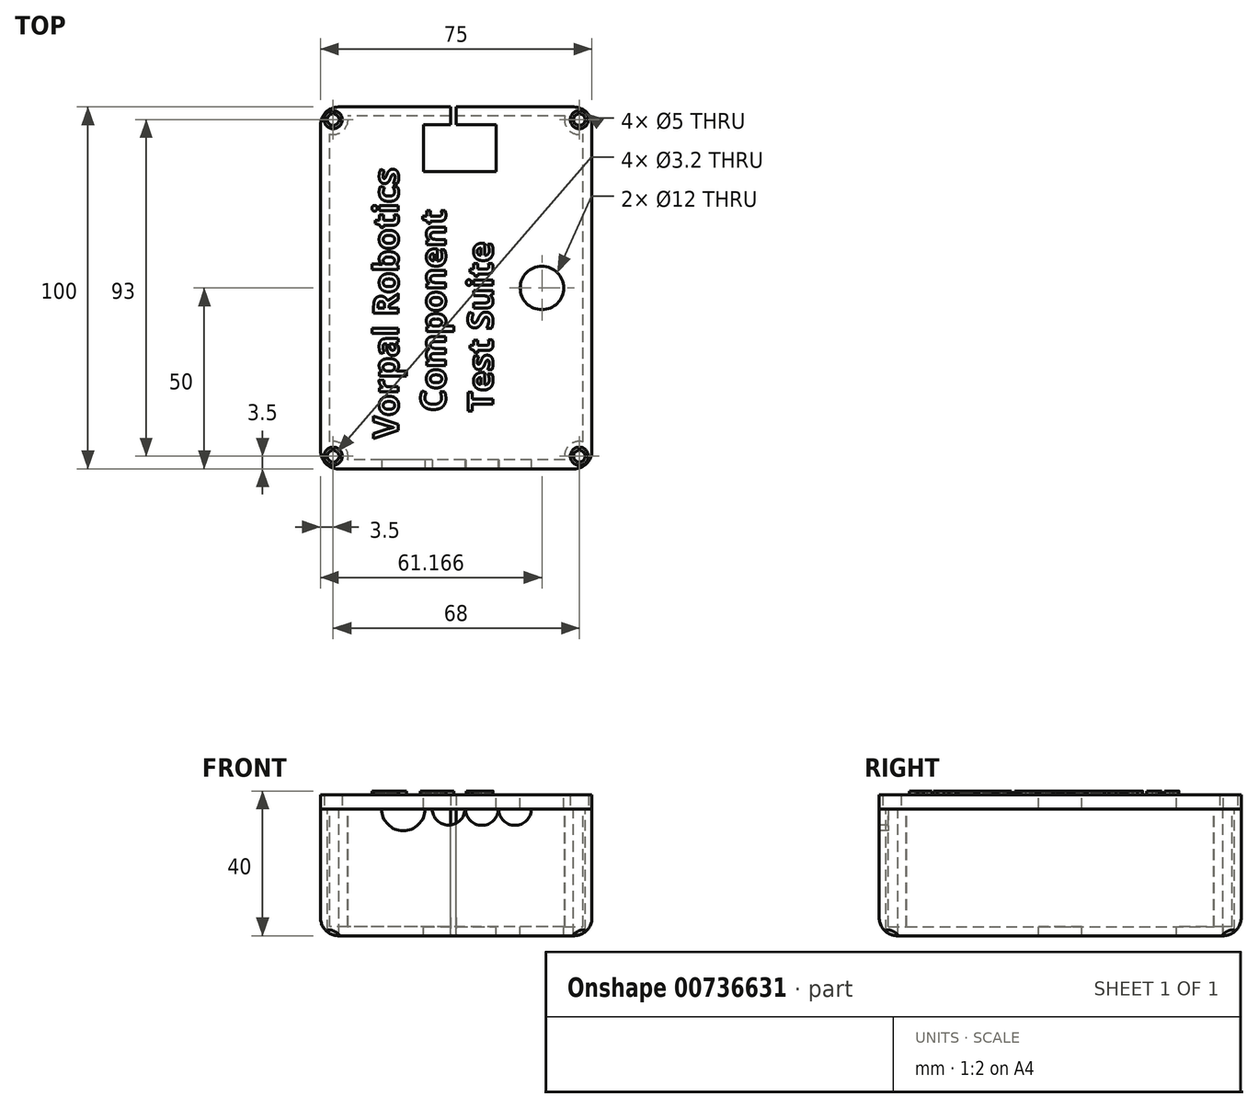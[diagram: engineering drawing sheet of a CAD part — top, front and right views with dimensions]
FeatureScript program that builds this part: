
annotation { "Feature Type Name" : "Feature", "Feature Type Description" : "" }
export const myFeature = defineFeature(function(context is Context, id is Id, definition is map)
    precondition{}
    {
        {
            var Q0;
            Q0=qCreatedBy(makeId("Top.planeOp"),FACE);
            var sketch = newSketch(context, id + "F0", { "sketchPlane" : qUnion([Q0])});
            skLineSegment(sketch, "E0.bottom", {"start": v(37.5, -50) * mm, "end": v(-37.5, -50) * mm});
            skLineSegment(sketch, "E0.top", {"start": v(37.5, 50) * mm, "end": v(-37.5, 50) * mm});
            skLineSegment(sketch, "E0.left", {"start": v(37.5, -50) * mm, "end": v(37.5, 50) * mm});
            skLineSegment(sketch, "E0.right", {"start": v(-37.5, -50) * mm, "end": v(-37.5, 50) * mm});
            skPoint(sketch, "E0.middle", {"position": v(0, 0) * mm});
            skLineSegment(sketch, "E1.bottom", {"start": v(34, -46.5) * mm, "end": v(-34, -46.5) * mm, "construction": true});
            skLineSegment(sketch, "E1.top", {"start": v(34, 46.5) * mm, "end": v(-34, 46.5) * mm, "construction": true});
            skLineSegment(sketch, "E1.left", {"start": v(34, -46.5) * mm, "end": v(34, 46.5) * mm, "construction": true});
            skLineSegment(sketch, "E1.right", {"start": v(-34, -46.5) * mm, "end": v(-34, 46.5) * mm, "construction": true});
            skCircle(sketch, "E2", {"center": v(-34, 46.5) * mm, "radius": 2.5 * mm});
            skCircle(sketch, "E3", {"center": v(34, 46.5) * mm, "radius": 2.5 * mm});
            skCircle(sketch, "E4", {"center": v(-34, -46.5) * mm, "radius": 2.5 * mm});
            skCircle(sketch, "E5", {"center": v(34, -46.5) * mm, "radius": 2.5 * mm});
            skCircle(sketch, "E6", {"center": v(-34, 46.5) * mm, "radius": 1.6 * mm});
            skCircle(sketch, "E7", {"center": v(34, 46.5) * mm, "radius": 1.6 * mm});
            skCircle(sketch, "E8", {"center": v(34, -46.5) * mm, "radius": 1.6 * mm});
            skCircle(sketch, "E9", {"center": v(-34, -46.5) * mm, "radius": 1.6 * mm});
            skSolve(sketch);
        }
        {
            var Q0;
            Q0 = qSketchRegion(id + "F0", true);
            var Q1;
            Q1=makeQuery(id+"F0.imprint","IMPRINT",FACE,{"disambiguationData":[TD([[makeQuery(id+"F0.imprint","IMPRINT",EDGE,{"derivedFrom":sQuery(id+"F0.wireOp",EDGE,"E2")}),1.0]])]});
            var Q2;
            Q2=makeQuery(id+"F0.imprint","IMPRINT",FACE,{"disambiguationData":[TD([[makeQuery(id+"F0.imprint","IMPRINT",EDGE,{"derivedFrom":sQuery(id+"F0.wireOp",EDGE,"E3")}),1.0]])]});
            var Q3;
            Q3=makeQuery(id+"F0.imprint","IMPRINT",FACE,{"disambiguationData":[TD([[makeQuery(id+"F0.imprint","IMPRINT",EDGE,{"derivedFrom":sQuery(id+"F0.wireOp",EDGE,"E4")}),1.0]])]});
            var Q4;
            Q4=makeQuery(id+"F0.imprint","IMPRINT",FACE,{"disambiguationData":[TD([[makeQuery(id+"F0.imprint","IMPRINT",EDGE,{"derivedFrom":sQuery(id+"F0.wireOp",EDGE,"E5")}),1.0]])]});
            extrude(context, id + "F1", {"entities" : qUnion([Q0, Q1, Q2, Q3, Q4]), "oppositeDirection" : true, "depth" : 35 * mm, "offsetDistance" : 25 * mm});
        }
        {
            var Q0;
            Q0=makeQuery(id+"F1.opExtrude","CAP_FACE",FACE,{"disambiguationData":[OSD([sQuery(id+"F0.wireOp",EDGE,"E0.bottom"),sQuery(id+"F0.wireOp",EDGE,"E0.top"),sQuery(id+"F0.wireOp",EDGE,"E0.left"),sQuery(id+"F0.wireOp",EDGE,"E0.right"),sQuery(id+"F0.wireOp",EDGE,"E6"),sQuery(id+"F0.wireOp",EDGE,"E7"),sQuery(id+"F0.wireOp",EDGE,"E8"),sQuery(id+"F0.wireOp",EDGE,"E9")])],"isStart":true});
            shell(context, id + "F2", {"entities" : qUnion([Q0]), "thickness" : 2.5 * mm});
        }
        {
            var Q0;
            Q0=makeQuery(id+"F1.opExtrude","SWEPT_EDGE",EDGE,{"disambiguationData":[OSD([sQuery(id+"F0.wireOp",EDGE,"E0.bottom"),sQuery(id+"F0.wireOp",EDGE,"E0.right")])]});
            var Q1;
            Q1=makeQuery(id+"F1.opExtrude","SWEPT_EDGE",EDGE,{"disambiguationData":[OSD([sQuery(id+"F0.wireOp",EDGE,"E0.bottom"),sQuery(id+"F0.wireOp",EDGE,"E0.left")])]});
            var Q2;
            Q2=makeQuery(id+"F1.opExtrude","SWEPT_EDGE",EDGE,{"disambiguationData":[OSD([sQuery(id+"F0.wireOp",EDGE,"E0.top"),sQuery(id+"F0.wireOp",EDGE,"E0.left")])]});
            var Q3;
            Q3=makeQuery(id+"F1.opExtrude","SWEPT_EDGE",EDGE,{"disambiguationData":[OSD([sQuery(id+"F0.wireOp",EDGE,"E0.top"),sQuery(id+"F0.wireOp",EDGE,"E0.right")])]});
            var Q4;
            Q4=makeQuery(id+"F1.opExtrude","CAP_EDGE",EDGE,{"disambiguationData":[OSD([sQuery(id+"F0.wireOp",EDGE,"E0.top")])],"isStart":false});
            var Q5;
            Q5=makeQuery(id+"F1.opExtrude","CAP_EDGE",EDGE,{"disambiguationData":[OSD([sQuery(id+"F0.wireOp",EDGE,"E0.right")])],"isStart":false});
            var Q6;
            Q6=makeQuery(id+"F1.opExtrude","CAP_EDGE",EDGE,{"disambiguationData":[OSD([sQuery(id+"F0.wireOp",EDGE,"E0.bottom")])],"isStart":false});
            var Q7;
            Q7=makeQuery(id+"F1.opExtrude","CAP_EDGE",EDGE,{"disambiguationData":[OSD([sQuery(id+"F0.wireOp",EDGE,"E0.left")])],"isStart":false});
            fillet(context, id + "F3", {"entities" : qUnion([Q0, Q1, Q2, Q3, Q4, Q5, Q6, Q7]), "radius" : 5 * mm, "allowEdgeOverflow" : false});
        }
        {
            var Q0;
            Q0=makeQuery(id+"F1.opExtrude","SWEPT_FACE",FACE,{"disambiguationData":[OSD([sQuery(id+"F0.wireOp",EDGE,"E0.bottom")])]});
            var sketch = newSketch(context, id + "F4", { "sketchPlane" : qUnion([Q0])});
            skCircle(sketch, "E10", {"center": v(-14.63, 0) * mm, "radius": 6 * mm});
            skCircle(sketch, "E11", {"center": v(-2.11, 0.07) * mm, "radius": 4.5 * mm});
            skCircle(sketch, "E12", {"center": v(7.1, 0) * mm, "radius": 4.5 * mm});
            skCircle(sketch, "E13", {"center": v(16.23, 0) * mm, "radius": 4.5 * mm});
            skSolve(sketch);
        }
        {
            var Q0;
            Q0 = qSketchRegion(id + "F4", true);
            extrude(context, id + "F5", {"entities" : qUnion([Q0]), "operationType" : NewBodyOperationType.REMOVE, "oppositeDirection" : true, "depth" : 25 * mm, "offsetDistance" : 25 * mm});
        }
        {
            var Q0;
            Q0 = qSketchRegion(id + "F0", true);
            extrude(context, id + "F6", {"entities" : qUnion([Q0]), "depth" : 4 * mm, "offsetDistance" : 25 * mm});
        }
        {
            var Q0;
            Q0=makeQuery(id+"F6.opExtrude","SWEPT_EDGE",EDGE,{"disambiguationData":[OSD([sQuery(id+"F0.wireOp",EDGE,"E0.bottom"),sQuery(id+"F0.wireOp",EDGE,"E0.right")])]});
            var Q1;
            Q1=makeQuery(id+"F6.opExtrude","SWEPT_EDGE",EDGE,{"disambiguationData":[OSD([sQuery(id+"F0.wireOp",EDGE,"E0.bottom"),sQuery(id+"F0.wireOp",EDGE,"E0.left")])]});
            var Q2;
            Q2=makeQuery(id+"F6.opExtrude","SWEPT_EDGE",EDGE,{"disambiguationData":[OSD([sQuery(id+"F0.wireOp",EDGE,"E0.top"),sQuery(id+"F0.wireOp",EDGE,"E0.left")])]});
            var Q3;
            Q3=makeQuery(id+"F6.opExtrude","SWEPT_EDGE",EDGE,{"disambiguationData":[OSD([sQuery(id+"F0.wireOp",EDGE,"E0.top"),sQuery(id+"F0.wireOp",EDGE,"E0.right")])]});
            fillet(context, id + "F7", {"entities" : qUnion([Q0, Q1, Q2, Q3]), "radius" : 5 * mm, "tangentPropagation" : true, "allowEdgeOverflow" : false});
        }
        {
            var Q0;
            Q0=makeQuery(id+"F6.opExtrude","CAP_FACE",FACE,{"disambiguationData":[OSD([sQuery(id+"F0.wireOp",EDGE,"E0.bottom"),sQuery(id+"F0.wireOp",EDGE,"E0.top"),sQuery(id+"F0.wireOp",EDGE,"E0.left"),sQuery(id+"F0.wireOp",EDGE,"E0.right"),sQuery(id+"F0.wireOp",EDGE,"E2"),sQuery(id+"F0.wireOp",EDGE,"E3"),sQuery(id+"F0.wireOp",EDGE,"E4"),sQuery(id+"F0.wireOp",EDGE,"E5")])],"isStart":false});
            var sketch = newSketch(context, id + "F8", { "sketchPlane" : qUnion([Q0])});
            skLineSegment(sketch, "E14.bottom", {"start": v(-8.99, 45.1) * mm, "end": v(-1.5, 45.1) * mm});
            skLineSegment(sketch, "E14.top", {"start": v(-8.99, 32.1) * mm, "end": v(11.01, 32.1) * mm});
            skLineSegment(sketch, "E14.left", {"start": v(-8.99, 45.1) * mm, "end": v(-8.99, 32.1) * mm});
            skLineSegment(sketch, "E14.right", {"start": v(11.01, 45.1) * mm, "end": v(11.01, 32.1) * mm});
            skLineSegment(sketch, "E15.bottom", {"start": v(-1.5, 53.63) * mm, "end": v(0, 53.63) * mm});
            skLineSegment(sketch, "E15.left", {"start": v(-1.5, 53.63) * mm, "end": v(-1.5, 45.1) * mm});
            skLineSegment(sketch, "E15.right", {"start": v(0, 53.63) * mm, "end": v(0, 45.1) * mm});
            skLineSegment(sketch, "E16.trimOffspring", {"start": v(0, 45.1) * mm, "end": v(11.01, 45.1) * mm});
            skCircle(sketch, "E17", {"center": v(23.67, 0) * mm, "radius": 6 * mm});
            skPoint(sketch, "E17.centerSnap0", {"position": v(37.5, 0) * mm});
            skSolve(sketch);
        }
        {
            var Q0;
            Q0 = qSketchRegion(id + "F8", true);
            extrude(context, id + "F9", {"entities" : qUnion([Q0]), "operationType" : NewBodyOperationType.REMOVE, "endBound" : BoundingType.THROUGH_ALL, "oppositeDirection" : true, "depth" : 25 * mm, "offsetDistance" : 25 * mm});
        }
        {
            var Q0;
            Q0=makeQuery(id+"F6.opExtrude","CAP_FACE",FACE,{"disambiguationData":[OSD([sQuery(id+"F0.wireOp",EDGE,"E0.bottom"),sQuery(id+"F0.wireOp",EDGE,"E0.top"),sQuery(id+"F0.wireOp",EDGE,"E0.left"),sQuery(id+"F0.wireOp",EDGE,"E0.right"),sQuery(id+"F0.wireOp",EDGE,"E2"),sQuery(id+"F0.wireOp",EDGE,"E3"),sQuery(id+"F0.wireOp",EDGE,"E4"),sQuery(id+"F0.wireOp",EDGE,"E5")])],"isStart":false});
            var sketch = newSketch(context, id + "F10", { "sketchPlane" : qUnion([Q0])});
            skText(sketch, "E18", { "text": "Vorpal Robotics\n   Component\n   Test Suite", "fontName": "OpenSans-Bold.ttf"});
            const initialGuessF10  = {"E18": [-0.01598, -0.04165, 0, 1, 0.0069]};
            skSetInitialGuess(sketch, initialGuessF10);
            skSolve(sketch);
        }
        {
            var Q0;
            Q0 = qSketchRegion(id + "F10", true);
            extrude(context, id + "F11", {"entities" : qUnion([Q0]), "operationType" : NewBodyOperationType.ADD, "depth" : 1 * mm, "offsetDistance" : 25 * mm});
        }
    });
